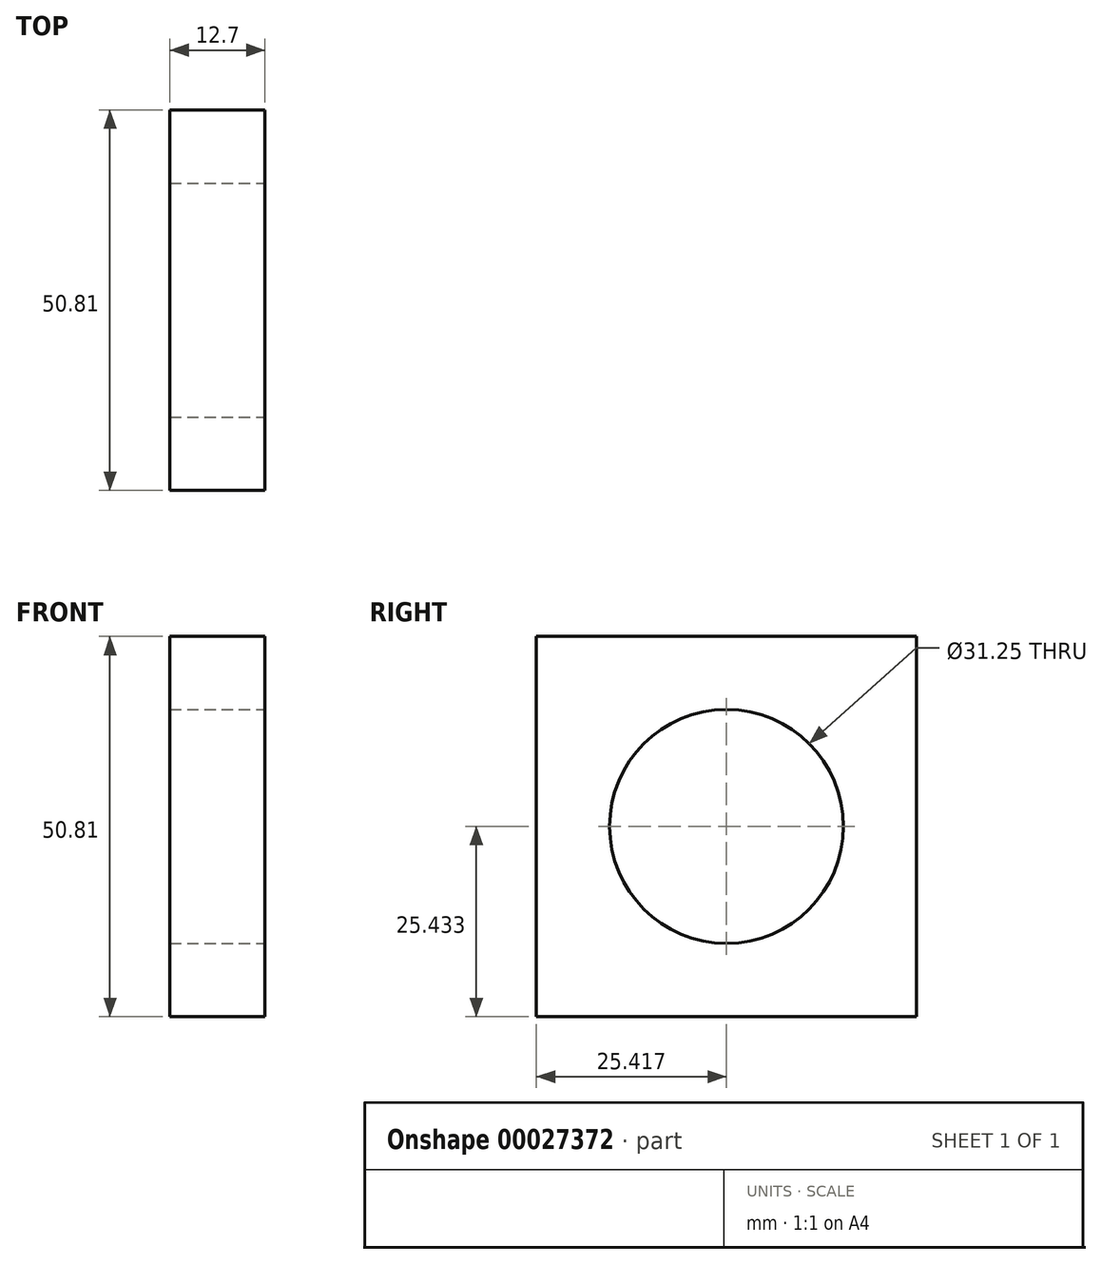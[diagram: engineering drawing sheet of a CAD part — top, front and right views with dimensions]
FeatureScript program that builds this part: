
annotation { "Feature Type Name" : "Feature", "Feature Type Description" : "" }
export const myFeature = defineFeature(function(context is Context, id is Id, definition is map)
    precondition{}
    {
        {
            var Q0;
            Q0=qCreatedBy(makeId("Top.planeOp"),FACE);
            var sketch = newSketch(context, id + "F0", { "sketchPlane" : qUnion([Q0])});
            skLineSegment(sketch, "E0.bottom", {"start": v(-36.63, -8.39) * mm, "end": v(17.03, -8.39) * mm});
            skLineSegment(sketch, "E0.top", {"start": v(-36.63, 37.49) * mm, "end": v(17.03, 37.49) * mm});
            skLineSegment(sketch, "E0.left", {"start": v(-36.63, -8.39) * mm, "end": v(-36.63, 37.49) * mm});
            skLineSegment(sketch, "E0.right", {"start": v(17.03, -8.39) * mm, "end": v(17.03, 37.49) * mm});
            skSolve(sketch);
        }
        {
            var Q0;
            Q0=makeQuery(id+"F0.imprint","IMPRINT",FACE,{"disambiguationData":[TD([[makeQuery(id+"F0.imprint","IMPRINT",EDGE,{"derivedFrom":sQuery(id+"F0.wireOp",EDGE,"E0.bottom")}),1.0]])]});
            extrude(context, id + "F1", {"entities" : qUnion([Q0]), "depth" : 25.4 * mm});
        }
        {
            var Q0;
            Q0=makeQuery(id+"F1.opExtrude","SWEPT_FACE",FACE,{"disambiguationData":[OSD([sQuery(id+"F0.wireOp",EDGE,"E0.top")])]});
            extrude(context, id + "F2", {"entities" : qUnion([Q0]), "operationType" : NewBodyOperationType.REMOVE, "oppositeDirection" : true, "depth" : 25.4 * mm});
        }
        {
            var Q0;
            Q0=makeQuery(id+"F1.opExtrude","CAP_EDGE",EDGE,{"disambiguationData":[OSD([sQuery(id+"F0.wireOp",EDGE,"E0.bottom")])],"isStart":false});
            fillet(context, id + "F3", {"entities" : qUnion([Q0]), "radius" : 12.7 * mm, "tangentPropagation" : true, "allowEdgeOverflow" : false});
        }
        {
            var Q0;
            Q0=makeQuery(id+"F1.opExtrude","SWEPT_BODY",BODY,{"disambiguationData":[OSD([sQuery(id+"F0.wireOp",EDGE,"E0.bottom"),sQuery(id+"F0.wireOp",EDGE,"E0.top"),sQuery(id+"F0.wireOp",EDGE,"E0.left"),sQuery(id+"F0.wireOp",EDGE,"E0.right")])]});
            deleteBodies(context, id + "F4", {"entities" : qUnion([Q0])});
        }
        {
            var Q0;
            Q0=qCreatedBy(makeId("Top.planeOp"),FACE);
            var sketch = newSketch(context, id + "F5", { "sketchPlane" : qUnion([Q0])});
            skLineSegment(sketch, "E1.bottom", {"start": v(0, 0) * mm, "end": v(54.8, 0) * mm});
            skLineSegment(sketch, "E1.top", {"start": v(0, -49.05) * mm, "end": v(54.8, -49.05) * mm});
            skLineSegment(sketch, "E1.left", {"start": v(0, 0) * mm, "end": v(0, -49.05) * mm});
            skLineSegment(sketch, "E1.right", {"start": v(54.8, 0) * mm, "end": v(54.8, -49.05) * mm});
            skSolve(sketch);
        }
        {
            var Q0;
            Q0=makeQuery(id+"F5.imprint","IMPRINT",FACE,{"disambiguationData":[TD([[makeQuery(id+"F5.imprint","IMPRINT",EDGE,{"derivedFrom":sQuery(id+"F5.wireOp",EDGE,"E1.bottom")}),-1.0]])]});
            extrude(context, id + "F6", {"entities" : qUnion([Q0]), "depth" : 12.7 * mm, "hasDraft" : true, "draftAngle" : 3 * degree});
        }
        {
            var Q0;
            Q0=makeQuery(id+"F6.opExtrude","SWEPT_FACE",FACE,{"disambiguationData":[OSD([sQuery(id+"F5.wireOp",EDGE,"E1.right")])]});
            extrude(context, id + "F7", {"entities" : qUnion([Q0]), "operationType" : NewBodyOperationType.ADD, "depth" : 25.4 * mm});
        }
        {
            var Q0;
            Q0=makeQuery(id+"F7.opExtrude","CAP_FACE",FACE,{"disambiguationData":[OSD([sQuery(id+"F5.wireOp",EDGE,"E1.right")])],"isStart":false});
            extrude(context, id + "F8", {"entities" : qUnion([Q0]), "operationType" : NewBodyOperationType.ADD, "depth" : 25.4 * mm});
        }
        {
            var Q0;
            Q0=makeQuery(id+"F8.opExtrude","CAP_FACE",FACE,{"disambiguationData":[OSD([sQuery(id+"F5.wireOp",EDGE,"E1.right")])],"isStart":false});
            extrude(context, id + "F9", {"entities" : qUnion([Q0]), "operationType" : NewBodyOperationType.REMOVE, "oppositeDirection" : true, "depth" : 25.4 * mm});
        }
        {
            var Q0;
            Q0=makeQuery(id+"F9.boolean.opBoolean","COPY",FACE,{"derivedFrom":makeQuery(id+"F9.opExtrude","CAP_FACE",FACE,{"disambiguationData":[OSD([sQuery(id+"F5.wireOp",EDGE,"E1.right")])],"isStart":false})});
            extrude(context, id + "F10", {"entities" : qUnion([Q0]), "operationType" : NewBodyOperationType.REMOVE, "oppositeDirection" : true, "depth" : 25.4 * mm});
        }
        {
            var Q0;
            Q0=makeQuery(id+"F10.boolean.opBoolean","COPY",FACE,{"derivedFrom":makeQuery(id+"F10.opExtrude","CAP_FACE",FACE,{"disambiguationData":[OSD([sQuery(id+"F5.wireOp",EDGE,"E1.right")])],"isStart":false})});
            extrude(context, id + "F11", {"entities" : qUnion([Q0]), "operationType" : NewBodyOperationType.REMOVE, "oppositeDirection" : true, "depth" : 5.33 * mm});
        }
        {
            var Q0;
            Q0=makeQuery(id+"F6.opExtrude","SWEPT_BODY",BODY,{"disambiguationData":[OSD([sQuery(id+"F5.wireOp",EDGE,"E1.bottom"),sQuery(id+"F5.wireOp",EDGE,"E1.top"),sQuery(id+"F5.wireOp",EDGE,"E1.left"),sQuery(id+"F5.wireOp",EDGE,"E1.right")])]});
            deleteBodies(context, id + "F12", {"entities" : qUnion([Q0])});
        }
        {
            var Q0;
            Q0=qCreatedBy(makeId("Right.planeOp"),FACE);
            var sketch = newSketch(context, id + "F13", { "sketchPlane" : qUnion([Q0])});
            skLineSegment(sketch, "E2.bottom", {"start": v(-42.8, 35.33) * mm, "end": v(-61.93, 35.33) * mm});
            skLineSegment(sketch, "E2.top", {"start": v(-42.8, 59.54) * mm, "end": v(-61.93, 59.54) * mm});
            skLineSegment(sketch, "E2.left", {"start": v(-42.8, 35.33) * mm, "end": v(-42.8, 59.54) * mm});
            skLineSegment(sketch, "E2.right", {"start": v(-61.93, 35.33) * mm, "end": v(-61.93, 59.54) * mm});
            skSolve(sketch);
        }
        {
            var Q0;
            Q0=makeQuery(id+"F13.imprint","IMPRINT",FACE,{"disambiguationData":[TD([[makeQuery(id+"F13.imprint","IMPRINT",EDGE,{"derivedFrom":sQuery(id+"F13.wireOp",EDGE,"E2.bottom")}),-1.0]])]});
            extrude(context, id + "F14", {"entities" : qUnion([Q0]), "depth" : 12.7 * mm});
        }
        {
            var Q0;
            Q0=makeQuery(id+"F14.opExtrude","SWEPT_FACE",FACE,{"disambiguationData":[OSD([sQuery(id+"F13.wireOp",EDGE,"E2.right")])]});
            extrude(context, id + "F15", {"entities" : qUnion([Q0]), "operationType" : NewBodyOperationType.ADD, "depth" : 37.34 * mm});
        }
        {
            var Q0;
            Q0=makeQuery(id+"F15.opExtrude","CAP_FACE",FACE,{"disambiguationData":[OSD([sQuery(id+"F13.wireOp",EDGE,"E2.right")])],"isStart":false});
            extrude(context, id + "F16", {"entities" : qUnion([Q0]), "operationType" : NewBodyOperationType.REMOVE, "oppositeDirection" : true, "depth" : 5.66 * mm});
        }
        {
            var Q0;
            {var subQ0=sQuery(id+"F13.wireOp",EDGE,"E2.top");Q0=makeQuery(id+"F15.boolean.opBoolean","MERGE",FACE,{"derivedFrom":[makeQuery(id+"F14.opExtrude","SWEPT_FACE",FACE,{"disambiguationData":[OSD([subQ0])]}),makeQuery(id+"F15.opExtrude","SWEPT_FACE",FACE,{"disambiguationData":[OSD([subQ0,sQuery(id+"F13.wireOp",EDGE,"E2.right")])]})]});}
            extrude(context, id + "F17", {"entities" : qUnion([Q0]), "operationType" : NewBodyOperationType.ADD, "depth" : 37.34 * mm});
        }
        {
            var Q0;
            Q0=makeQuery(id+"F17.opExtrude","CAP_FACE",FACE,{"disambiguationData":[OSD([sQuery(id+"F13.wireOp",EDGE,"E2.top"),sQuery(id+"F13.wireOp",EDGE,"E2.right")])],"isStart":false});
            extrude(context, id + "F18", {"entities" : qUnion([Q0]), "operationType" : NewBodyOperationType.REMOVE, "oppositeDirection" : true, "depth" : 10.74 * mm});
        }
        {
            var Q0;
            {var subQ0=sQuery(id+"F13.wireOp",EDGE,"E2.top");var subQ1=sQuery(id+"F13.wireOp",EDGE,"E2.right");Q0=makeQuery(id+"F17.boolean.opBoolean","MERGE",FACE,{"derivedFrom":[makeQuery(id+"F15.boolean.opBoolean","MERGE",FACE,{"derivedFrom":[makeQuery(id+"F14.opExtrude","CAP_FACE",FACE,{"disambiguationData":[OSD([sQuery(id+"F13.wireOp",EDGE,"E2.bottom"),subQ0,sQuery(id+"F13.wireOp",EDGE,"E2.left"),subQ1])],"isStart":false}),makeQuery(id+"F15.opExtrude","SWEPT_FACE",FACE,{"disambiguationData":[OSD([subQ1]),TDD([makeQuery(id+"F14.opExtrude","CAP_EDGE",EDGE,{"disambiguationData":[OSD([subQ1])],"isStart":false})])]})]}),makeQuery(id+"F17.opExtrude","SWEPT_FACE",FACE,{"disambiguationData":[OSD([subQ0,subQ1]),TDD([makeQuery(id+"F15.boolean.opBoolean","MERGE",EDGE,{"derivedFrom":[makeQuery(id+"F14.opExtrude","CAP_EDGE",EDGE,{"disambiguationData":[OSD([subQ0])],"isStart":false}),makeQuery(id+"F15.opExtrude","SWEPT_EDGE",EDGE,{"disambiguationData":[OSD([subQ0,subQ1]),TDD([makeQuery(id+"F14.opExtrude","CAP_VERTEX",VERTEX,{"disambiguationData":[OSD([subQ0,subQ1])],"isStart":false})])]})]})])]})]});}
            var sketch = newSketch(context, id + "F19", { "sketchPlane" : qUnion([Q0])});
            skLineSegment(sketch, "E3", {"start": v(-93.6, 35.33) * mm, "end": v(-42.8, 86.14) * mm});
            skLineSegment(sketch, "E4", {"start": v(-42.8, 86.14) * mm, "end": v(-93.6, 86.14) * mm});
            skLineSegment(sketch, "E5", {"start": v(-93.6, 86.14) * mm, "end": v(-42.8, 35.33) * mm});
            skSolve(sketch);
        }
        {
            var Q0;
            {var subQ5=sQuery(id+"F19.wireOp",EDGE,"E4");Q0=makeQuery(id+"F19.imprint","IMPRINT",FACE,{"disambiguationData":[TD([[makeQuery(id+"F19.imprint","IMPRINT",EDGE,{"derivedFrom":subQ5}),1.0]])]});}
            var sketch = newSketch(context, id + "F20", { "sketchPlane" : qUnion([Q0])});
            skCircle(sketch, "E6", {"center": v(-68.2, 60.76) * mm, "radius": 15.62 * mm});
            skSolve(sketch);
        }
        {
            var Q0;
            {var subQ0=sQuery(id+"F19.wireOp",EDGE,"E5");var subQ1=sQuery(id+"F19.wireOp",EDGE,"E3");var subQ2=makeQuery(id+"F19.imprint","INTERSECT",VERTEX,{"derivedFrom":[subQ1,subQ0]});var subQ7=sQuery(id+"F20.wireOp",EDGE,"E6");var subQ10=makeQuery(id+"F19.imprint","IMPRINT",EDGE,{"disambiguationData":[TD([[subQ2,-1.0]])],"derivedFrom":subQ1});var subQ12=makeQuery(id+"F20.imprint","INTERSECT",VERTEX,{"derivedFrom":[subQ10,subQ7]});Q0=makeQuery(id+"F20.imprint","IMPRINT",FACE,{"disambiguationData":[TD([[makeQuery(id+"F20.imprint","IMPRINT",EDGE,{"disambiguationData":[TD([[subQ12,-1.0]])],"derivedFrom":subQ7}),1.0]])]});}
            var Q1;
            {var subQ0=sQuery(id+"F19.wireOp",EDGE,"E5");var subQ1=sQuery(id+"F19.wireOp",EDGE,"E3");var subQ2=makeQuery(id+"F19.imprint","INTERSECT",VERTEX,{"derivedFrom":[subQ1,subQ0]});var subQ7=sQuery(id+"F20.wireOp",EDGE,"E6");var subQ10=makeQuery(id+"F19.imprint","IMPRINT",EDGE,{"disambiguationData":[TD([[subQ2,-1.0]])],"derivedFrom":subQ1});var subQ12=makeQuery(id+"F20.imprint","INTERSECT",VERTEX,{"derivedFrom":[subQ10,subQ7]});Q1=makeQuery(id+"F20.imprint","IMPRINT",FACE,{"disambiguationData":[TD([[makeQuery(id+"F20.imprint","IMPRINT",EDGE,{"disambiguationData":[TD([[subQ12,1.0]])],"derivedFrom":subQ7}),1.0]])]});}
            extrude(context, id + "F21", {"entities" : qUnion([Q0, Q1]), "operationType" : NewBodyOperationType.REMOVE, "oppositeDirection" : true, "depth" : 25.4 * mm});
        }
    });
